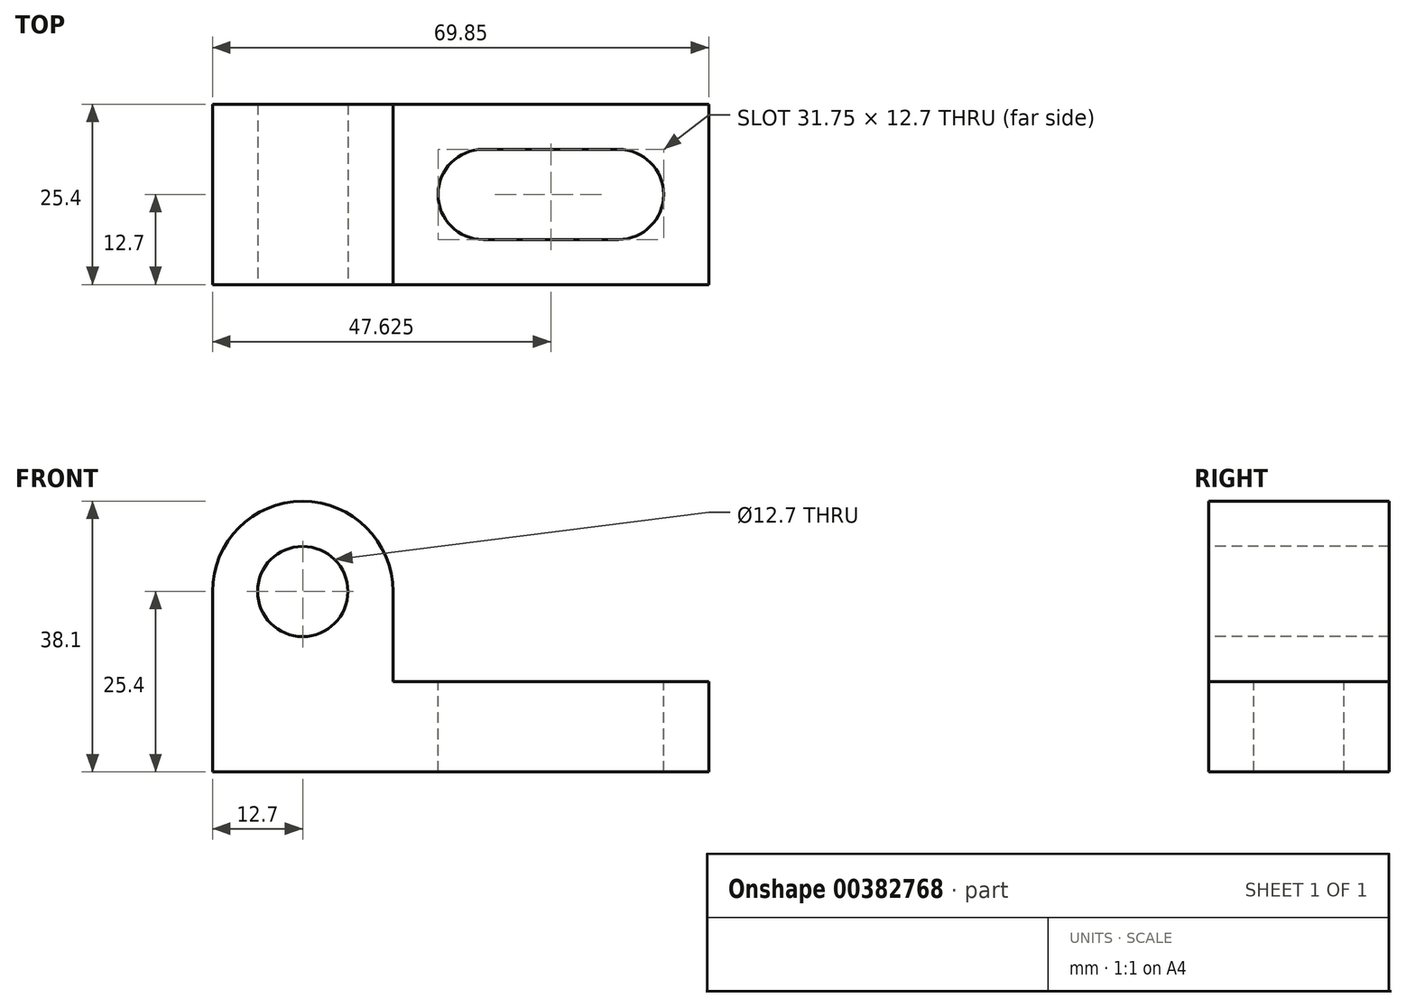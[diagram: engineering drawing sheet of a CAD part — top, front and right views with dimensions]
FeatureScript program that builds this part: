
annotation { "Feature Type Name" : "Feature", "Feature Type Description" : "" }
export const myFeature = defineFeature(function(context is Context, id is Id, definition is map)
    precondition{}
    {
        {
            var Q0;
            Q0=qCreatedBy(makeId("Front.planeOp"),FACE);
            var sketch = newSketch(context, id + "F0", { "sketchPlane" : qUnion([Q0])});
            skLineSegment(sketch, "E0.bottom", {"start": v(0, 0) * mm, "end": v(-69.85, 0) * mm});
            skLineSegment(sketch, "E0.top", {"start": v(0, 38.1) * mm, "end": v(-69.85, 38.1) * mm});
            skLineSegment(sketch, "E0.left", {"start": v(0, 0) * mm, "end": v(0, 38.1) * mm});
            skLineSegment(sketch, "E0.right", {"start": v(-69.85, 0) * mm, "end": v(-69.85, 38.1) * mm});
            skSolve(sketch);
        }
        {
            var Q0;
            Q0=makeQuery(id+"F0.imprint","IMPRINT",FACE,{"disambiguationData":[TD([[makeQuery(id+"F0.imprint","IMPRINT",EDGE,{"derivedFrom":sQuery(id+"F0.wireOp",EDGE,"E0.bottom")}),-1.0]])]});
            extrude(context, id + "F1", {"entities" : qUnion([Q0]), "depth" : 25.4 * mm});
        }
        {
            var Q0;
            Q0=qCreatedBy(makeId("Front.planeOp"),FACE);
            var sketch = newSketch(context, id + "F2", { "sketchPlane" : qUnion([Q0])});
            skLineSegment(sketch, "E1", {"start": v(-44.45, 38.1) * mm, "end": v(-44.45, 12.7) * mm});
            skLineSegment(sketch, "E2", {"start": v(-44.45, 12.7) * mm, "end": v(0, 12.7) * mm});
            skLineSegment(sketch, "E3", {"start": v(0, 12.7) * mm, "end": v(0, 38.1) * mm});
            skLineSegment(sketch, "E4", {"start": v(0, 38.1) * mm, "end": v(-44.45, 38.1) * mm});
            skSolve(sketch);
        }
        {
            var Q0;
            Q0 = qSketchRegion(id + "F2", true);
            extrude(context, id + "F3", {"entities" : qUnion([Q0]), "operationType" : NewBodyOperationType.REMOVE, "depth" : 31.75 * mm});
        }
        {
            var Q0;
            Q0=makeQuery(id+"F3.boolean.opBoolean","COPY",FACE,{"derivedFrom":makeQuery(id+"F3.opExtrude","SWEPT_FACE",FACE,{"disambiguationData":[OSD([sQuery(id+"F2.wireOp",EDGE,"E2")])]})});
            var sketch = newSketch(context, id + "F4", { "sketchPlane" : qUnion([Q0])});
            skCircle(sketch, "E5", {"center": v(-12.7, -12.7) * mm, "radius": 6.35 * mm});
            skCircle(sketch, "E6", {"center": v(-31.75, -12.7) * mm, "radius": 6.35 * mm});
            skLineSegment(sketch, "E7", {"start": v(-31.75, -6.35) * mm, "end": v(-12.7, -6.35) * mm});
            skLineSegment(sketch, "E8", {"start": v(-12.7, -6.35) * mm, "end": v(-31.75, -6.35) * mm});
            skLineSegment(sketch, "E9", {"start": v(-12.7, -19.05) * mm, "end": v(-31.75, -19.05) * mm});
            skLineSegment(sketch, "E10", {"start": v(-31.75, -19.05) * mm, "end": v(-12.7, -19.05) * mm});
            skSolve(sketch);
        }
        {
            var Q0;
            Q0 = qSketchRegion(id + "F4", true);
            extrude(context, id + "F5", {"entities" : qUnion([Q0]), "operationType" : NewBodyOperationType.REMOVE, "oppositeDirection" : true, "depth" : 25.4 * mm});
        }
        {
            var Q0;
            Q0=makeQuery(id+"F1.opExtrude","CAP_FACE",FACE,{"disambiguationData":[OSD([sQuery(id+"F0.wireOp",EDGE,"E0.bottom"),sQuery(id+"F0.wireOp",EDGE,"E0.top"),sQuery(id+"F0.wireOp",EDGE,"E0.left"),sQuery(id+"F0.wireOp",EDGE,"E0.right")])],"isStart":false});
            var sketch = newSketch(context, id + "F6", { "sketchPlane" : qUnion([Q0])});
            skCircle(sketch, "E11", {"center": v(-57.15, 25.4) * mm, "radius": 6.35 * mm});
            skArc(sketch, "E12", {"start": v(-44.45, 25.4) * mm, "mid": v(-57.15, 38.1) * mm, "end": v(-69.85, 25.4) * mm});
            skSolve(sketch);
        }
        {
            var Q0;
            Q0 = qSketchRegion(id + "F6", true);
            var Q1;
            {var subQ0=sQuery(id+"F6.wireOp",EDGE,"E12");var subQ1=sQuery(id+"F0.wireOp",EDGE,"E0.top");var subQ4=makeQuery(id+"F1.opExtrude","CAP_EDGE",EDGE,{"disambiguationData":[OSD([subQ1])],"isStart":false});var subQ5=makeQuery(id+"F6.imprint","INTERSECT",VERTEX,{"derivedFrom":[subQ4,subQ0]});Q1=makeQuery(id+"F6.imprint","IMPRINT",FACE,{"disambiguationData":[TD([[makeQuery(id+"F6.imprint","IMPRINT",EDGE,{"disambiguationData":[TD([[subQ5,1.0]])],"derivedFrom":subQ0}),-1.0]])]});}
            var Q2;
            {var subQ0=sQuery(id+"F6.wireOp",EDGE,"E12");var subQ1=makeQuery(id+"F1.opExtrude","CAP_EDGE",EDGE,{"disambiguationData":[OSD([sQuery(id+"F0.wireOp",EDGE,"E0.right")])],"isStart":false});var subQ2=makeQuery(id+"F6.imprint","INTERSECT",VERTEX,{"derivedFrom":[subQ1,subQ0]});Q2=makeQuery(id+"F6.imprint","IMPRINT",FACE,{"disambiguationData":[TD([[makeQuery(id+"F6.imprint","IMPRINT",EDGE,{"disambiguationData":[TD([[subQ2,1.0]])],"derivedFrom":subQ0}),-1.0]])]});}
            extrude(context, id + "F7", {"entities" : qUnion([Q0, Q1, Q2]), "operationType" : NewBodyOperationType.REMOVE, "oppositeDirection" : true, "depth" : 31.75 * mm});
        }
    });
